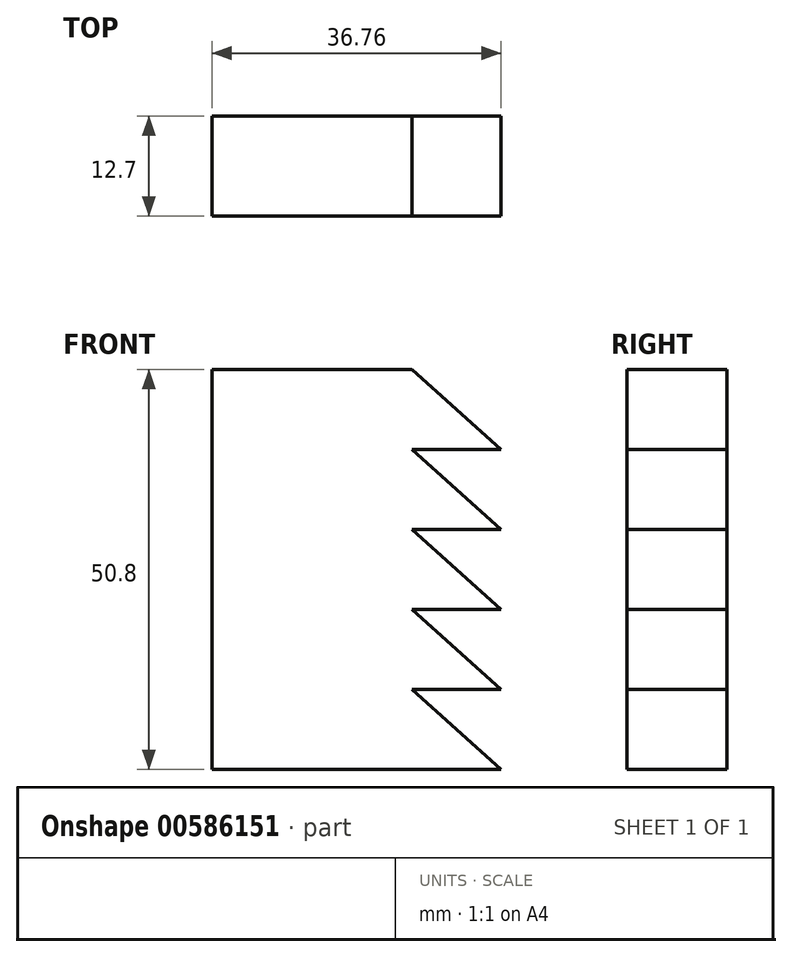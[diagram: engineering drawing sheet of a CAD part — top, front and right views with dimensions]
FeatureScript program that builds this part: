
annotation { "Feature Type Name" : "Feature", "Feature Type Description" : "" }
export const myFeature = defineFeature(function(context is Context, id is Id, definition is map)
    precondition{}
    {
        {
            var Q0;
            Q0=qCreatedBy(makeId("Front.planeOp"),FACE);
            var sketch = newSketch(context, id + "F0", { "sketchPlane" : qUnion([Q0])});
            skLineSegment(sketch, "E0", {"start": v(0, 50.8) * mm, "end": v(0, 0) * mm});
            skLineSegment(sketch, "E1", {"start": v(0, 0) * mm, "end": v(0, 50.8) * mm});
            skLineSegment(sketch, "E2", {"start": v(0, 50.8) * mm, "end": v(11.36, 40.64) * mm});
            skLineSegment(sketch, "E3", {"start": v(11.36, 40.64) * mm, "end": v(0, 40.64) * mm});
            skLineSegment(sketch, "E4", {"start": v(0, 40.64) * mm, "end": v(11.36, 30.48) * mm});
            skLineSegment(sketch, "E5", {"start": v(11.36, 30.48) * mm, "end": v(0, 30.48) * mm});
            skLineSegment(sketch, "E6", {"start": v(0, 30.48) * mm, "end": v(11.36, 20.32) * mm});
            skLineSegment(sketch, "E7", {"start": v(11.36, 20.32) * mm, "end": v(0, 20.32) * mm});
            skLineSegment(sketch, "E8", {"start": v(0, 20.32) * mm, "end": v(11.36, 10.16) * mm});
            skLineSegment(sketch, "E9", {"start": v(11.36, 10.16) * mm, "end": v(0, 10.16) * mm});
            skLineSegment(sketch, "E10", {"start": v(0, 10.16) * mm, "end": v(11.36, 0) * mm});
            skLineSegment(sketch, "E11", {"start": v(11.36, 0) * mm, "end": v(0, 0) * mm});
            skLineSegment(sketch, "E12", {"start": v(0, 50.8) * mm, "end": v(-25.4, 50.8) * mm});
            skLineSegment(sketch, "E13", {"start": v(-25.4, 50.8) * mm, "end": v(-25.4, 0) * mm});
            skLineSegment(sketch, "E14", {"start": v(-25.4, 0) * mm, "end": v(0, 0) * mm});
            skSolve(sketch);
        }
        {
            var Q0;
            Q0 = qSketchRegion(id + "F0", true);
            extrude(context, id + "F1", {"entities" : qUnion([Q0]), "depth" : 12.7 * mm, "offsetDistance" : 25.4 * mm});
        }
    });
